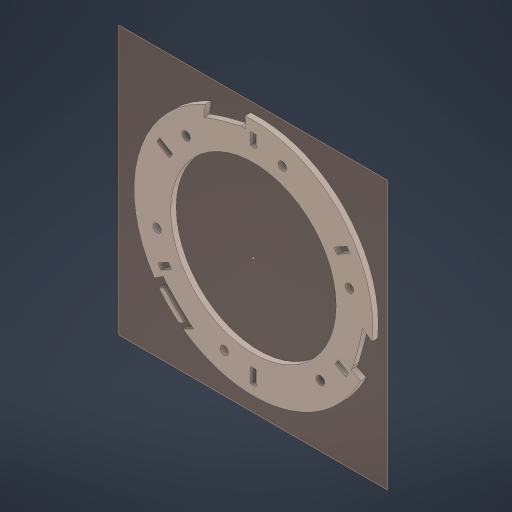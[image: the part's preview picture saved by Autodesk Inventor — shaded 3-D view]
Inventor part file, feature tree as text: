
AUTODESK INVENTOR PART (.ipt)
format: ipt  version: 2023 (Build 270158000, 158)  size: 350,208 bytes
history: native  units: mm
features: reference x17, other x10, sketch x5, extrude x4, pattern_circular x2, plane x1, projected_geometry x1
ambient origin geometry x8: Origin, YZ Plane, XZ Plane, XY Plane, X Axis, Y Axis, Z Axis, Center Point
bodies: Solid1 (feature_tree)
feature tree (40):
  plane  "Work Plane1"
  extrude  "Extrusion1"  Depth=3.0mm TaperAngle=0.0deg
  sketch  "Sketch2"  dims[d3=1.5mm d4=3.0mm d5=0.0mm d6=30.0mm d7=360.0deg]
  extrude  "Extrusion2"  Depth=3.0mm TaperAngle=0.0deg
  pattern_circular  "Circular Pattern1"  Count=3 Angle=360.0deg
  extrude  "Extrusion3"  Depth=10.0mm
  extrude  "Extrusion4"  Depth=10.0mm TaperAngle=360.0deg
  pattern_circular  "Circular Pattern2"  [2 undecoded]
  sketch  "Sketch1"  dims[d0=90.0mm d1=3.0mm d2=0.0mm]
  reference  "Reference1"
  reference  "Reference2"
  reference  "Reference3"
  reference  "Reference4"
  reference  "Reference5"
  reference  "Reference6"
  reference  "Reference7"
  reference  "Reference8"
  reference  "Reference9"
  reference  "Reference10"
  reference  "Reference11"
  reference  "Reference12"
  reference  "Reference13"
  sketch  "Sketch3"  dims[d9=10.0mm d10=0.0mm d11=4.5mm]
  reference  "Reference14"
  sketch  "Sketch4"  dims[d12=10.0mm d13=0.0mm d14=60.0mm d15=360.0deg]
  reference  "Reference15"
  reference  "Reference16"
  projected_geometry  "Projected Loop1"
  reference  "Reference17"
  sketch  "Sketch5"
  parser-record x1  (decoder bookkeeping rows leaked as tree rows — omitted from the tree; the rows remain in map.json)
  other  "Assembly1.iam"
  other  "vase_v2._tom:1"
  other  "Spant:3"
  other  "Spant:2"
  other  "Spant:1"
  other  "Spant2:2"
  other  "Spant2:3"
  other  "Spant2:1"
  other  "Assembly1"
note: 2 required parameter values undecoded (feature->parameter linkage not recoverable at this tier; creation-order binding heuristic only, values carry confidence <= 0.55)
note: 1 file-system path scrubbed to <path> (originals preserved in map.json)
